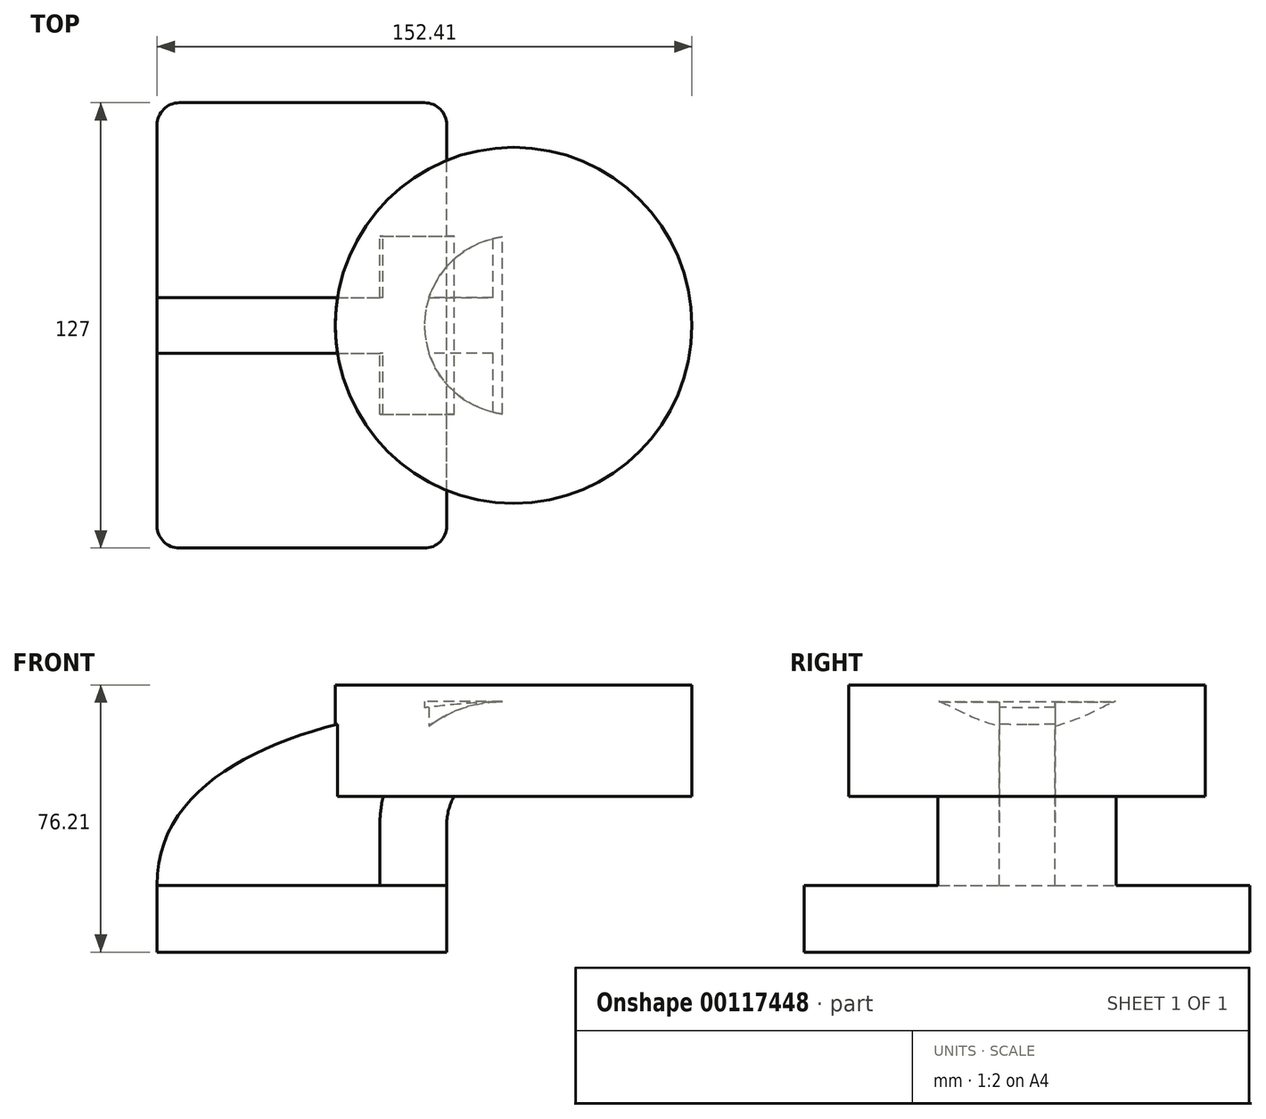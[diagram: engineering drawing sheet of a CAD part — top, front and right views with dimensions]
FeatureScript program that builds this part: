
annotation { "Feature Type Name" : "Feature", "Feature Type Description" : "" }
export const myFeature = defineFeature(function(context is Context, id is Id, definition is map)
    precondition{}
    {
        {
            var Q0;
            Q0=qCreatedBy(makeId("Front.planeOp"),FACE);
            var sketch = newSketch(context, id + "F0", { "sketchPlane" : qUnion([Q0])});
            skLineSegment(sketch, "E0.bottom", {"start": v(-41.28, 9.52) * mm, "end": v(41.27, 9.53) * mm});
            skLineSegment(sketch, "E0.top", {"start": v(-41.28, -9.53) * mm, "end": v(41.28, -9.53) * mm});
            skLineSegment(sketch, "E0.left", {"start": v(-41.28, 9.52) * mm, "end": v(-41.27, -9.53) * mm});
            skLineSegment(sketch, "E0.right", {"start": v(41.28, 9.53) * mm, "end": v(41.28, -9.52) * mm});
            skPoint(sketch, "E0.middle", {"position": v(0, 0) * mm});
            skLineSegment(sketch, "E1", {"start": v(41.27, 9.53) * mm, "end": v(41.27, 27) * mm});
            skLineSegment(sketch, "E2.bottom", {"start": v(60.32, 34.92) * mm, "end": v(111.12, 34.92) * mm});
            skLineSegment(sketch, "E2.top", {"start": v(60.32, 66.68) * mm, "end": v(111.12, 66.68) * mm});
            skLineSegment(sketch, "E2.left", {"start": v(60.32, 34.92) * mm, "end": v(60.32, 66.67) * mm});
            skLineSegment(sketch, "E2.right", {"start": v(111.12, 34.92) * mm, "end": v(111.12, 66.67) * mm});
            skPoint(sketch, "E2.middle", {"position": v(85.72, 50.8) * mm});
            skArc(sketch, "E3", {"start": v(41.27, 27) * mm, "mid": v(45.92, 38.23) * mm, "end": v(57.15, 42.88) * mm});
            skLineSegment(sketch, "E4", {"start": v(57.15, 42.88) * mm, "end": v(85.72, 42.88) * mm});
            skPoint(sketch, "E4.endSnap0", {"position": v(85.72, 34.92) * mm});
            skLineSegment(sketch, "E5.0", {"start": v(57.15, 61.93) * mm, "end": v(85.72, 61.93) * mm});
            skArc(sketch, "E5.1", {"start": v(22.22, 27) * mm, "mid": v(32.45, 51.7) * mm, "end": v(57.15, 61.93) * mm});
            skLineSegment(sketch, "E5.2", {"start": v(22.22, 9.53) * mm, "end": v(22.22, 27) * mm});
            skLineSegment(sketch, "E6", {"start": v(85.72, 42.88) * mm, "end": v(85.72, 61.93) * mm});
            skFitSpline(sketch, "E7", {"points": [v(-41.28, 9.53) * mm, v(57.15, 61.93) * mm], "startDerivative": vector(-1.63, 118.44) * mm, "endDerivative": vector(114.45, 3.74) * mm});
            skSolve(sketch);
        }
        {
            var Q0;
            Q0=makeQuery(id+"F0.imprint","IMPRINT",FACE,{"disambiguationData":[TD([[makeQuery(id+"F0.imprint","IMPRINT",EDGE,{"derivedFrom":sQuery(id+"F0.wireOp",EDGE,"E0.top")}),1.0]])]});
            extrude(context, id + "F1", {"entities" : qUnion([Q0]), "endBound" : BoundingType.SYMMETRIC, "depth" : 127 * mm});
        }
        {
            var Q0;
            {var subQ1=sQuery(id+"F0.wireOp",EDGE,"E1");Q0=makeQuery(id+"F0.imprint","IMPRINT",FACE,{"disambiguationData":[TD([[makeQuery(id+"F0.imprint","IMPRINT",EDGE,{"derivedFrom":subQ1}),1.0]])]});}
            var Q1;
            {var subQ5=sQuery(id+"F0.wireOp",EDGE,"E6");Q1=makeQuery(id+"F0.imprint","IMPRINT",FACE,{"disambiguationData":[TD([[makeQuery(id+"F0.imprint","IMPRINT",EDGE,{"derivedFrom":subQ5}),1.0]])]});}
            extrude(context, id + "F2", {"entities" : qUnion([Q0, Q1]), "operationType" : NewBodyOperationType.ADD, "endBound" : BoundingType.SYMMETRIC, "depth" : 50.8 * mm});
        }
        {
            var Q0;
            {var subQ3=sQuery(id+"F0.wireOp",EDGE,"E5.2");Q0=makeQuery(id+"F0.imprint","IMPRINT",FACE,{"disambiguationData":[TD([[makeQuery(id+"F0.imprint","IMPRINT",EDGE,{"derivedFrom":subQ3}),1.0]])]});}
            extrude(context, id + "F3", {"entities" : qUnion([Q0]), "operationType" : NewBodyOperationType.ADD, "endBound" : BoundingType.SYMMETRIC, "depth" : 15.88 * mm});
        }
        {
            var Q0;
            Q0=makeQuery(id+"F1.opExtrude","CAP_EDGE",EDGE,{"disambiguationData":[OSD([sQuery(id+"F0.wireOp",EDGE,"E0.left")])],"isStart":false});
            var Q1;
            Q1=makeQuery(id+"F1.opExtrude","CAP_EDGE",EDGE,{"disambiguationData":[OSD([sQuery(id+"F0.wireOp",EDGE,"E0.right")])],"isStart":false});
            var Q2;
            Q2=makeQuery(id+"F1.opExtrude","CAP_EDGE",EDGE,{"disambiguationData":[OSD([sQuery(id+"F0.wireOp",EDGE,"E0.right")])],"isStart":true});
            var Q3;
            Q3=makeQuery(id+"F1.opExtrude","CAP_EDGE",EDGE,{"disambiguationData":[OSD([sQuery(id+"F0.wireOp",EDGE,"E0.left")])],"isStart":true});
            fillet(context, id + "F4", {"entities" : qUnion([Q0, Q1, Q2, Q3]), "radius" : 6.35 * mm, "tangentPropagation" : true, "allowEdgeOverflow" : false});
        }
        {
            var Q0;
            {var subQ4=sQuery(id+"F0.wireOp",EDGE,"E2.bottom");Q0=makeQuery(id+"F0.imprint","IMPRINT",FACE,{"disambiguationData":[TD([[makeQuery(id+"F0.imprint","IMPRINT",EDGE,{"derivedFrom":subQ4}),1.0]])]});}
            var Q1;
            Q1=sQuery(id+"F0.wireOp",EDGE,"E2.left");
            revolve(context, id + "F5", {"operationType" : NewBodyOperationType.ADD, "entities" : qUnion([Q0]), "axis" : qUnion([Q1]), "revolveType" : RevolveType.FULL});
        }
    });
